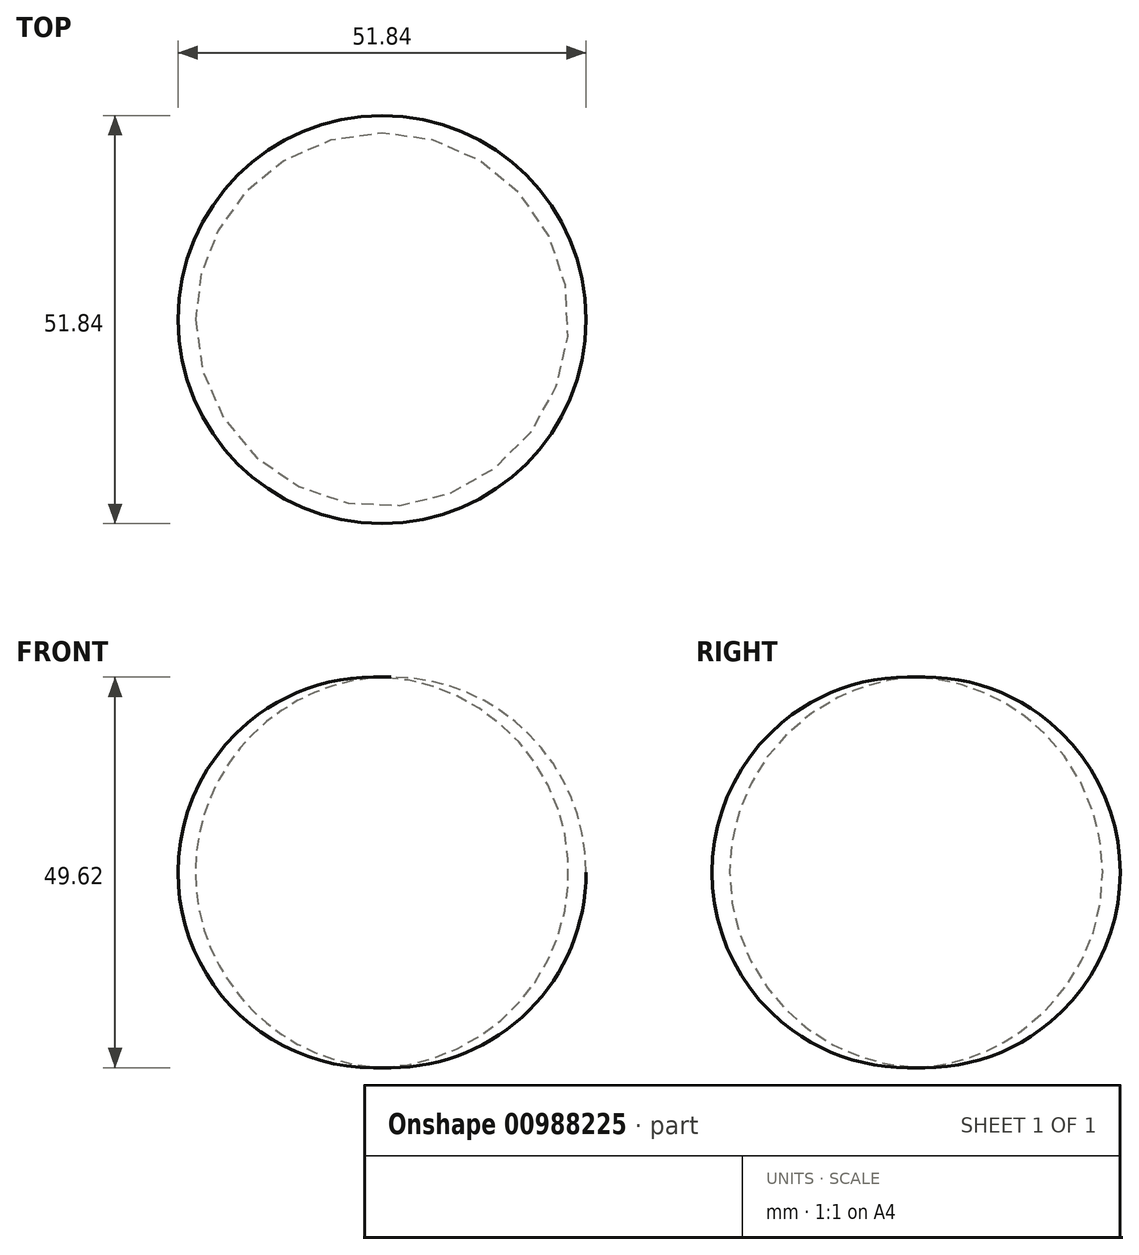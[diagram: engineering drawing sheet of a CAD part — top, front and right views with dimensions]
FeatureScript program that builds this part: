
annotation { "Feature Type Name" : "Feature", "Feature Type Description" : "" }
export const myFeature = defineFeature(function(context is Context, id is Id, definition is map)
    precondition{}
    {
        {
            var Q0;
            Q0=qCreatedBy(makeId("Front.planeOp"),FACE);
            var sketch = newSketch(context, id + "F0", { "sketchPlane" : qUnion([Q0])});
            skLineSegment(sketch, "E0", {"start": v(0, 25.35) * mm, "end": v(0, -24.22) * mm});
            skArc(sketch, "E1", {"start": v(0, -24.22) * mm, "mid": v(25.92, 0.57) * mm, "end": v(0, 25.35) * mm});
            skSolve(sketch);
        }
        {
            var Q0;
            Q0=makeQuery(id+"F0.imprint","IMPRINT",FACE,{"disambiguationData":[TD([[makeQuery(id+"F0.imprint","IMPRINT",EDGE,{"derivedFrom":sQuery(id+"F0.wireOp",EDGE,"E0")}),1.0]])]});
            var Q1;
            Q1=sQuery(id+"F0.wireOp",EDGE,"E0");
            revolve(context, id + "F1", {"surfaceOperationType" : NewSurfaceOperationType.NEW, "entities" : qUnion([Q0]), "axis" : qUnion([Q1]), "revolveType" : RevolveType.FULL});
        }
    });
